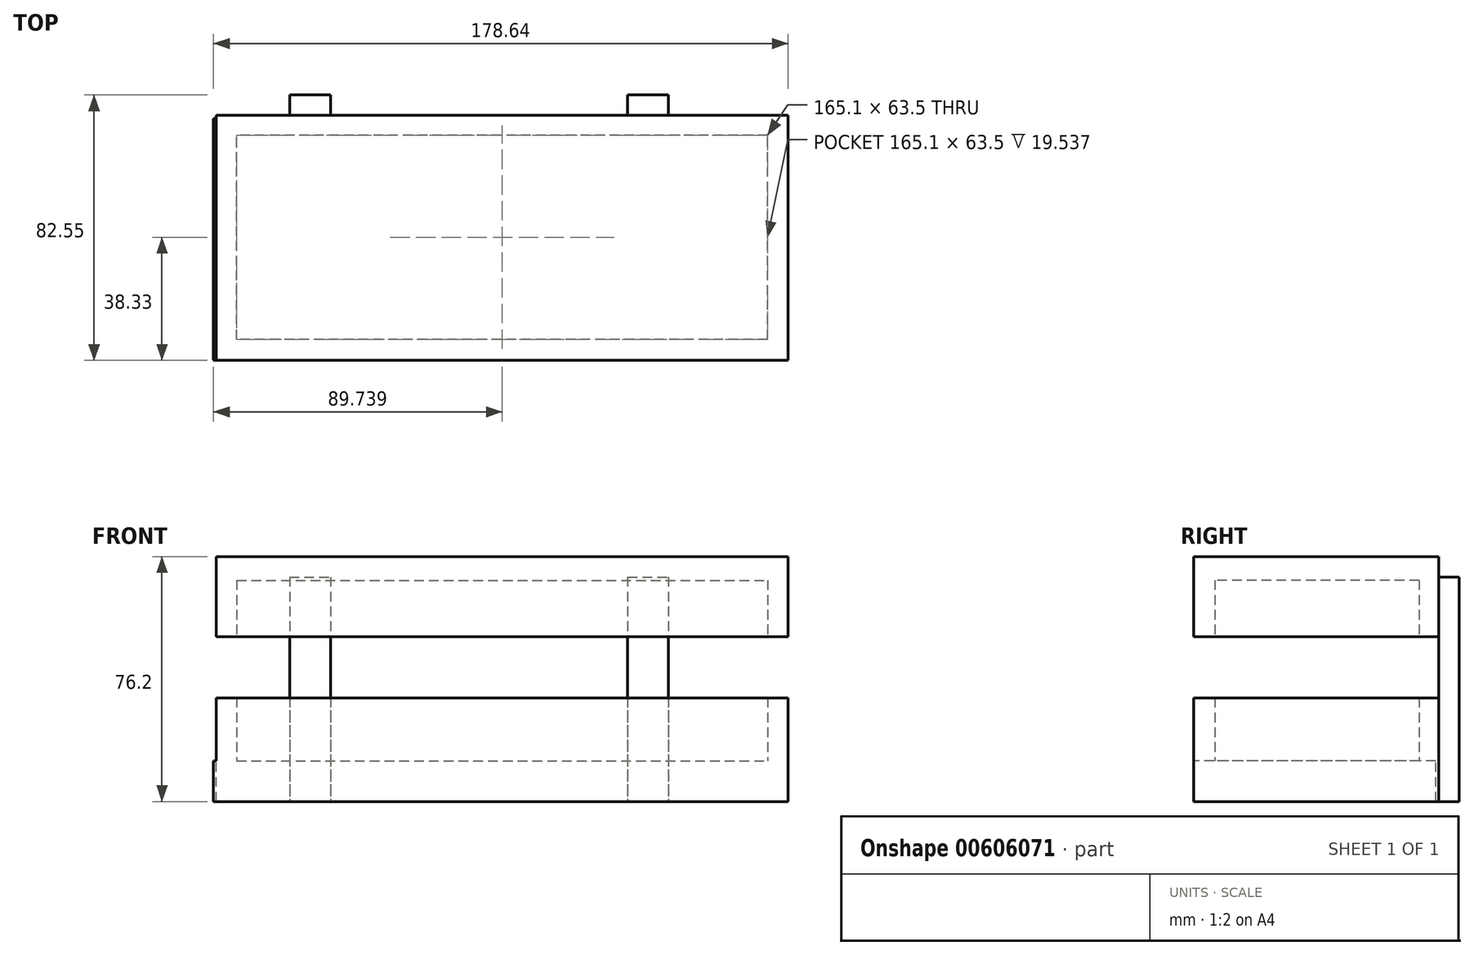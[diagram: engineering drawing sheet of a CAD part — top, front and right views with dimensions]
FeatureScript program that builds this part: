
annotation { "Feature Type Name" : "Feature", "Feature Type Description" : "" }
export const myFeature = defineFeature(function(context is Context, id is Id, definition is map)
    precondition{}
    {
        {
            var Q0;
            Q0=qCreatedBy(makeId("Top.planeOp"),FACE);
            var sketch = newSketch(context, id + "F0", { "sketchPlane" : qUnion([Q0])});
            skLineSegment(sketch, "E0.bottom", {"start": v(-108.36, 76.2) * mm, "end": v(69.44, 76.2) * mm});
            skLineSegment(sketch, "E0.top", {"start": v(-108.36, 0) * mm, "end": v(69.44, 0) * mm});
            skLineSegment(sketch, "E0.left", {"start": v(-108.36, 76.2) * mm, "end": v(-108.36, 0) * mm});
            skLineSegment(sketch, "E0.right", {"start": v(69.44, 76.2) * mm, "end": v(69.44, 0) * mm});
            skSolve(sketch);
        }
        {
            var Q0;
            Q0 = qSketchRegion(id + "F0", true);
            extrude(context, id + "F1", {"entities" : qUnion([Q0]), "depth" : 76.2 * mm, "offsetDistance" : 25.4 * mm});
        }
        {
            var Q0;
            Q0=qCreatedBy(makeId("Top.planeOp"),FACE);
            var sketch = newSketch(context, id + "F2", { "sketchPlane" : qUnion([Q0])});
            skLineSegment(sketch, "E1.bottom", {"start": v(-102.01, 70.08) * mm, "end": v(63.09, 70.08) * mm});
            skLineSegment(sketch, "E1.top", {"start": v(-102.01, 6.58) * mm, "end": v(63.09, 6.58) * mm});
            skLineSegment(sketch, "E1.left", {"start": v(-102.01, 70.08) * mm, "end": v(-102.01, 6.58) * mm});
            skLineSegment(sketch, "E1.right", {"start": v(63.09, 70.08) * mm, "end": v(63.09, 6.58) * mm});
            skSolve(sketch);
        }
        {
            var Q0;
            Q0 = qSketchRegion(id + "F2", true);
            extrude(context, id + "F3", {"entities" : qUnion([Q0]), "operationType" : NewBodyOperationType.REMOVE, "depth" : 68.83 * mm, "offsetDistance" : 25.4 * mm});
        }
        {
            var Q0;
            Q0=qCreatedBy(makeId("Front.planeOp"),FACE);
            var sketch = newSketch(context, id + "F4", { "sketchPlane" : qUnion([Q0])});
            skLineSegment(sketch, "E2.bottom", {"start": v(-123.97, 51.29) * mm, "end": v(85.58, 51.29) * mm});
            skLineSegment(sketch, "E2.top", {"start": v(-123.97, 32.24) * mm, "end": v(85.58, 32.24) * mm});
            skLineSegment(sketch, "E2.left", {"start": v(-123.97, 51.29) * mm, "end": v(-123.97, 32.24) * mm});
            skLineSegment(sketch, "E2.right", {"start": v(85.58, 51.29) * mm, "end": v(85.58, 32.24) * mm});
            skSolve(sketch);
        }
        {
            var Q0;
            Q0 = qSketchRegion(id + "F4", true);
            extrude(context, id + "F5", {"entities" : qUnion([Q0]), "operationType" : NewBodyOperationType.REMOVE, "oppositeDirection" : true, "depth" : 87.12 * mm, "offsetDistance" : 25.4 * mm});
        }
        {
            var Q0;
            Q0=qCreatedBy(makeId("Top.planeOp"),FACE);
            var sketch = newSketch(context, id + "F6", { "sketchPlane" : qUnion([Q0])});
            skLineSegment(sketch, "E3.bottom", {"start": v(-109.2, 0) * mm, "end": v(68.93, 0) * mm});
            skLineSegment(sketch, "E3.top", {"start": v(-109.2, 75.28) * mm, "end": v(68.93, 75.28) * mm});
            skLineSegment(sketch, "E3.left", {"start": v(-109.2, 0) * mm, "end": v(-109.2, 75.28) * mm});
            skLineSegment(sketch, "E3.right", {"start": v(68.93, 0) * mm, "end": v(68.93, 75.28) * mm});
            skSolve(sketch);
        }
        {
            var Q0;
            Q0 = qSketchRegion(id + "F6", true);
            extrude(context, id + "F7", {"entities" : qUnion([Q0]), "operationType" : NewBodyOperationType.ADD, "depth" : 12.7 * mm, "offsetDistance" : 25.4 * mm});
        }
        {
            var Q0;
            Q0=makeQuery(id+"F7.boolean.opBoolean","MERGE",FACE,{"derivedFrom":[makeQuery(id+"F1.opExtrude","CAP_FACE",FACE,{"disambiguationData":[OSD([sQuery(id+"F0.wireOp",EDGE,"E0.bottom"),sQuery(id+"F0.wireOp",EDGE,"E0.top"),sQuery(id+"F0.wireOp",EDGE,"E0.left"),sQuery(id+"F0.wireOp",EDGE,"E0.right")])],"isStart":true}),makeQuery(id+"F7.opExtrude","CAP_FACE",FACE,{"disambiguationData":[OSD([sQuery(id+"F6.wireOp",EDGE,"E3.bottom"),sQuery(id+"F6.wireOp",EDGE,"E3.top"),sQuery(id+"F6.wireOp",EDGE,"E3.left"),sQuery(id+"F6.wireOp",EDGE,"E3.right")])],"isStart":true})]});
            var sketch = newSketch(context, id + "F8", { "sketchPlane" : qUnion([Q0])});
            skLineSegment(sketch, "E4.bottom", {"start": v(-85.56, -76.2) * mm, "end": v(-72.86, -76.2) * mm});
            skLineSegment(sketch, "E4.top", {"start": v(-85.56, -82.55) * mm, "end": v(-72.86, -82.55) * mm});
            skLineSegment(sketch, "E4.left", {"start": v(-85.56, -76.2) * mm, "end": v(-85.56, -82.55) * mm});
            skLineSegment(sketch, "E4.right", {"start": v(-72.86, -76.2) * mm, "end": v(-72.86, -82.55) * mm});
            skLineSegment(sketch, "E5.bottom", {"start": v(19.58, -76.2) * mm, "end": v(32.29, -76.2) * mm});
            skLineSegment(sketch, "E5.top", {"start": v(19.58, -82.55) * mm, "end": v(32.29, -82.55) * mm});
            skLineSegment(sketch, "E5.left", {"start": v(19.58, -76.2) * mm, "end": v(19.58, -82.55) * mm});
            skLineSegment(sketch, "E5.right", {"start": v(32.29, -76.2) * mm, "end": v(32.29, -82.55) * mm});
            skSolve(sketch);
        }
        {
            var Q0;
            Q0 = qSketchRegion(id + "F8", true);
            extrude(context, id + "F9", {"entities" : qUnion([Q0]), "operationType" : NewBodyOperationType.ADD, "oppositeDirection" : true, "depth" : 69.85 * mm, "offsetDistance" : 25.4 * mm});
        }
    });
